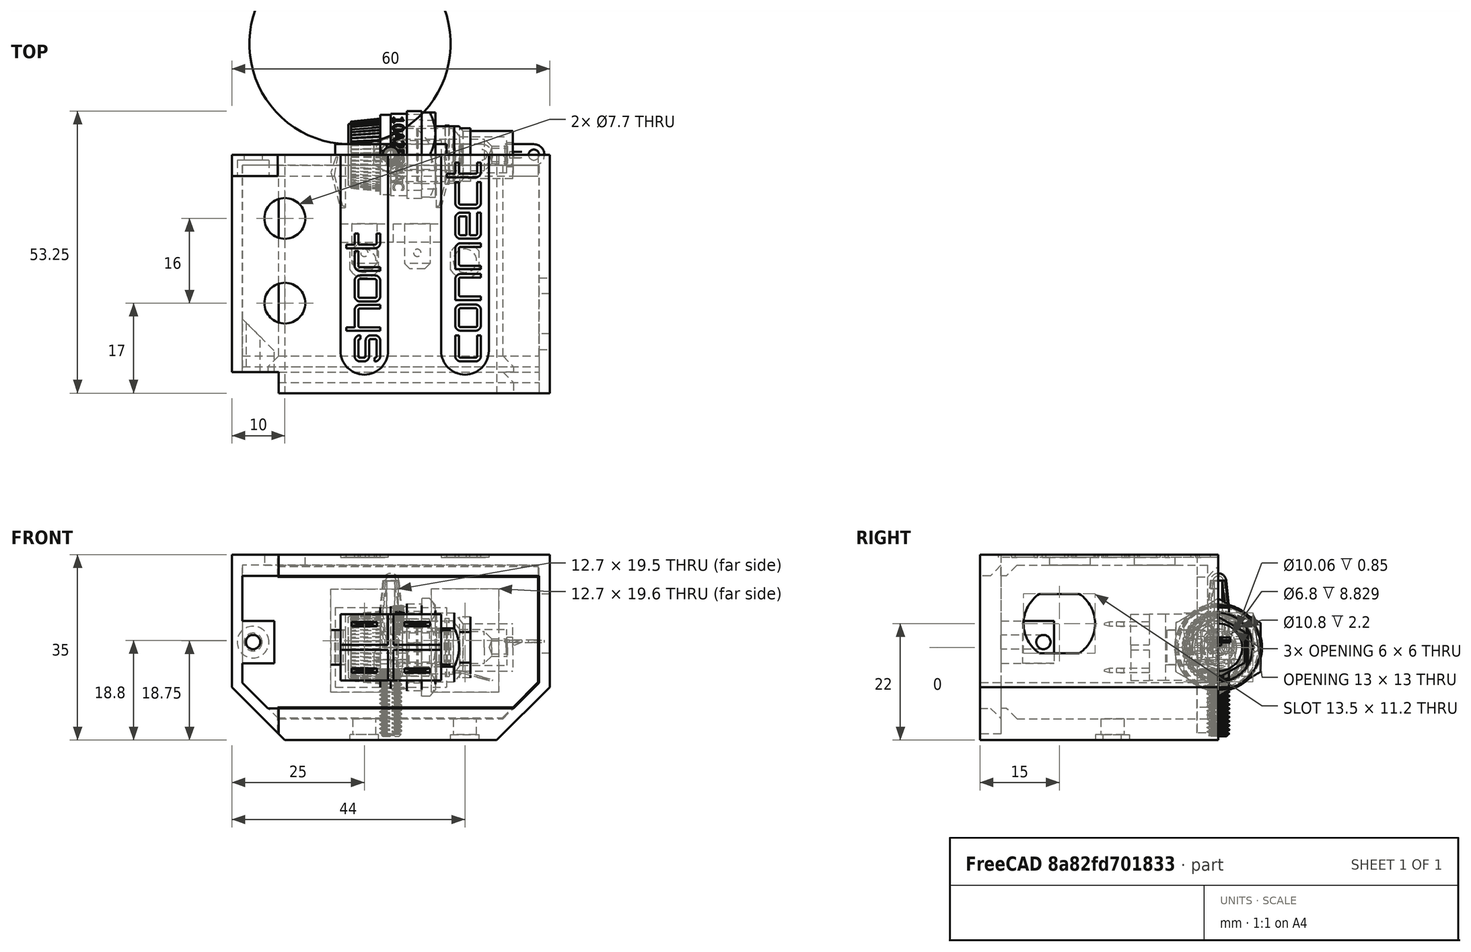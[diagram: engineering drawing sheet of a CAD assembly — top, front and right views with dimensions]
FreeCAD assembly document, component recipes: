
FREECAD ASSEMBLY — COMPONENT RECIPES ("multimeter_module")

This assembly document has 9 components, labeled P0..P8 below (a component is one placed body or linked part). 9 of them carry a construction recipe — the FreeCAD feature program that regenerates the part from scratch, quoted from this document or its linked companion documents; the rest are supplied as boundary geometry only. No exploded tour is included for this assembly.
COMPONENT P0 — recipe-attached ("Box001", modeled in this document).
Construction recipe (the document's own serialized feature program — sketch geometry with constraints, then the solid features built on it; lengths are millimeters unless a unit is written):

FEATURE [Sketcher::SketchObject] Sketch
  ArcFitTolerance = 1e-06
  AttachmentSupport = -> [XZ_Plane]
  FullyConstrained = true
  MakeInternals = false
  MapMode = 5
  Placement = pos=(0,0,0) rot=(1,0,0;1.5708rad)
  expr: Constraints[10] = Spreadsheet.Height
  expr: Constraints[9] = Spreadsheet.Length
  sketch-geometry (5):
    g0: LineSegment StartX=-30 StartY=-17.5 StartZ=0 EndX=30 EndY=-17.5 EndZ=0
    g1: LineSegment StartX=30 StartY=-17.5 StartZ=0 EndX=30 EndY=17.5 EndZ=0
    g2: LineSegment StartX=30 StartY=17.5 StartZ=0 EndX=-30 EndY=17.5 EndZ=0
    g3: LineSegment StartX=-30 StartY=17.5 StartZ=0 EndX=-30 EndY=-17.5 EndZ=0
    g4: GeomPoint [constr] X=0 Y=0 Z=0
  constraints (12):
    c: Coincident(g0,g1)
    c: Coincident(g1,g2)
    c: Coincident(g2,g3)
    c: Coincident(g3,g0)
    c: Horizontal(g0)
    c: Horizontal(g2)
    c: Vertical(g1)
    c: Vertical(g3)
    c: Symmetric(g2,g0,g4)
    c: Distance(g1,g3) = 60
    c: Distance(g0,g2) = 35
    c: Coincident(g4,g-1)
FEATURE [PartDesign::Pad] Pad
  Direction = (0,-1,2e-16)
  Length = 45
  Length2 = 10
  Placement = pos=(0,0,0) rot=(1,0,0;1.5708rad)
  Profile = -> Sketch
  ReferenceAxis = -> Sketch [N_Axis]
  Refine = true
  Suppressed = false
  Type = 0
  expr: Length = Spreadsheet.Width
FEATURE [Sketcher::SketchObject] Sketch001
  ArcFitTolerance = 1e-06
  AttachmentSupport = -> [Pad]
  ExternalGeometry = -> [Pad]
  FullyConstrained = true
  MakeInternals = false
  MapMode = 5
  Placement = pos=(0,-45,0) rot=(1,0,0;1.5708rad)
  expr: Constraints[10] = Spreadsheet.Length - 2 * Spreadsheet.Thickness
  expr: Constraints[11] = Spreadsheet.Thickness
  expr: Constraints[12] = Spreadsheet.Thickness
  expr: Constraints[9] = Spreadsheet.Height - Spreadsheet.Thickness - Spreadsheet.ThicknessBottom
  sketch-geometry (5):
    g0: LineSegment StartX=28 StartY=-13.5 StartZ=0 EndX=28 EndY=15.5 EndZ=0
    g1: LineSegment StartX=28 StartY=15.5 StartZ=0 EndX=-28 EndY=15.5 EndZ=0
    g2: LineSegment StartX=-28 StartY=15.5 StartZ=0 EndX=-28 EndY=-13.5 EndZ=0
    g3: LineSegment StartX=-28 StartY=-13.5 StartZ=0 EndX=28 EndY=-13.5 EndZ=0
    g4: GeomPoint [constr] X=0 Y=0 Z=0
  constraints (13):
    c: Coincident(g0,g1)
    c: Coincident(g1,g2)
    c: Coincident(g2,g3)
    c: Coincident(g3,g0)
    c: Vertical(g0)
    c: Vertical(g2)
    c: Horizontal(g1)
    c: Horizontal(g3)
    c: Coincident(g4,g-1)
    c: DistanceY(g0,g0) = 29
    c: DistanceX(g3,g3) = 56
    c: Distance(g-4,g1) = 2
    c: Distance(g-3,g2) = 2
FEATURE [PartDesign::Pocket] Pocket  label="Box inside"
  BaseFeature = -> Pad
  Direction = (0,1,-2e-16)
  Length = 43
  Length2 = 5
  Placement = pos=(0,0,0) rot=(1,0,0;1.5708rad)
  Profile = -> Sketch001
  ReferenceAxis = -> Sketch001 [N_Axis]
  Refine = true
  Suppressed = false
  Type = 0
  expr: Length = Spreadsheet.Width - Spreadsheet.Thickness
FEATURE [Sketcher::SketchObject] Sketch003
  ArcFitTolerance = 1e-06
  AttachmentSupport = -> [Pocket]
  ExternalGeometry = -> [Pocket]
  FullyConstrained = true
  MakeInternals = false
  MapMode = 5
  Placement = pos=(0,0,0) rot=(-1,0,0;1.5708rad)
  expr: Constraints[19] = Spreadsheet.SwitchWidth
  expr: Constraints[21] = Spreadsheet.SwitchDistance
  expr: Constraints[26] = Spreadsheet.PlugOffset
  expr: Constraints[8] = Spreadsheet.SwitchWidth
  expr: Constraints[9] = Spreadsheet.SwitchHeight
  sketch-geometry (11):
    g0: LineSegment StartX=7.65 StartY=-11.1 StartZ=0 EndX=20.35 EndY=-11.1 EndZ=0
    g1: LineSegment StartX=20.35 StartY=-11.1 StartZ=0 EndX=20.35 EndY=8.5 EndZ=0
    g2: LineSegment StartX=20.35 StartY=8.5 StartZ=0 EndX=7.65 EndY=8.5 EndZ=0
    g3: LineSegment StartX=7.65 StartY=8.5 StartZ=0 EndX=7.65 EndY=-11.1 EndZ=0
    g4: GeomPoint [constr] X=14 Y=-1.3 Z=0
    g5: LineSegment StartX=-11.35 StartY=-11 StartZ=0 EndX=1.35 EndY=-11 EndZ=0
    g6: LineSegment StartX=1.35 StartY=-11 StartZ=0 EndX=1.35 EndY=8.5 EndZ=0
    g7: LineSegment StartX=1.35 StartY=8.5 StartZ=0 EndX=-11.35 EndY=8.5 EndZ=0
    g8: LineSegment StartX=-11.35 StartY=8.5 StartZ=0 EndX=-11.35 EndY=-11 EndZ=0
    g9: GeomPoint [constr] X=-5 Y=-1.25 Z=0
    g10: LineSegment [constr] StartX=-11.35 StartY=8.5 StartZ=0 EndX=20.35 EndY=8.5 EndZ=0
  constraints (28):
    c: Coincident(g0,g1)
    c: Coincident(g1,g2)
    c: Coincident(g2,g3)
    c: Coincident(g3,g0)
    c: Horizontal(g0)
    c: Horizontal(g2)
    c: Vertical(g1)
    c: Vertical(g3)
    c: Distance(g1,g3) = 12.7
    c: Distance(g0,g2) = 19.6
    c: Coincident(g5,g6)
    c: Coincident(g6,g7)
    c: Coincident(g7,g8)
    c: Coincident(g8,g5)
    c: Horizontal(g5)
    c: Horizontal(g7)
    c: Vertical(g6)
    c: Vertical(g8)
    c: Symmetric(g7,g5,g9) = 13
    c: Distance(g6,g8) = 12.7
    c: Distance(g5,g7) = 19.5
    c: DistanceX(g9,g4) = 19
    c: Distance(g-3,g7) = 9
    c: Coincident(g10,g7)
    c: Coincident(g10,g1)
    c: Horizontal(g10)
    c: Distance(g4,g-4) = 16
    c: Symmetric(g0,g1,g4)
FEATURE [PartDesign::Pocket] Pocket001  label="Switch holes"
  BaseFeature = -> Pocket
  Direction = (0,-1,-2e-16)
  Length = 3
  Length2 = 5
  Placement = pos=(0,0,0) rot=(1,0,0;1.5708rad)
  Profile = -> Sketch003
  ReferenceAxis = -> Sketch003 [N_Axis]
  Refine = true
  Suppressed = false
  Type = 0
  expr: Length = Spreadsheet.Thickness + 1
FEATURE [Sketcher::SketchObject] Sketch004
  ArcFitTolerance = 1e-06
  AttachmentSupport = -> [Pocket001]
  ExternalGeometry = -> [Pocket001]
  FullyConstrained = true
  MakeInternals = false
  MapMode = 5
  Placement = pos=(0,-7.7e-15,-17.5) rot=(1,0,0;3.14159rad)
  expr: Constraints[0] = Spreadsheet.PlugDiameter
  expr: Constraints[1] = Spreadsheet.PlugDiameter
  expr: Constraints[5] = Spreadsheet.PlugOffset
  expr: Constraints[7] = Spreadsheet.PlugDistance
  sketch-geometry (3):
    g0: Circle CenterX=14 CenterY=20 CenterZ=0 NormalX=0 NormalY=0 NormalZ=1 AngleXU=0 Radius=2.2
    g1: Circle CenterX=-5 CenterY=20 CenterZ=0 NormalX=0 NormalY=0 NormalZ=1 AngleXU=0 Radius=2.2
    g2: LineSegment [constr] StartX=-5 StartY=20 StartZ=0 EndX=14 EndY=20 EndZ=0
  constraints (8):
    c: Diameter(g0) = 4.4
    c: Diameter(g1) = 4.4
    c: Coincident(g2,g1)
    c: Coincident(g2,g0)
    c: Horizontal(g2)
    c: Distance(g0,g-4) = 16
    c: DistanceY(g-1,g0) = 20
    c: DistanceX(g1,g0) = 19
FEATURE [PartDesign::Pocket] Pocket002  label="Plug holes"
  BaseFeature = -> Pocket001
  Direction = (0,0,1)
  Length = 5
  Length2 = 5
  Placement = pos=(0,0,0) rot=(1,0,0;1.5708rad)
  Profile = -> Sketch004
  ReferenceAxis = -> Sketch004 [N_Axis]
  Refine = true
  Suppressed = false
  Type = 0
  expr: Length = Spreadsheet.ThicknessBottom + 1
FEATURE [Sketcher::SketchObject] Sketch005
  ArcFitTolerance = 1e-06
  AttachmentSupport = -> [Pocket002]
  ExternalGeometry = -> [Pocket002]
  FullyConstrained = true
  MakeInternals = false
  MapMode = 5
  Placement = pos=(0,7.7e-15,17.5) rot=(0,0,1;3.14159rad)
  expr: Constraints[0] = Spreadsheet.SocketDiameter
  expr: Constraints[1] = Spreadsheet.SocketDiameter
  expr: Constraints[5] = Spreadsheet.SocketDistance
  sketch-geometry (3):
    g0: Circle CenterX=20 CenterY=28 CenterZ=0 NormalX=0 NormalY=0 NormalZ=1 AngleXU=0 Radius=3.85
    g1: Circle CenterX=20 CenterY=12 CenterZ=0 NormalX=0 NormalY=0 NormalZ=1 AngleXU=0 Radius=3.85
    g2: LineSegment [constr] StartX=20 StartY=28 StartZ=0 EndX=20 EndY=12 EndZ=0
  constraints (8):
    c: Diameter(g0) = 7.7
    c: Diameter(g1) = 7.7
    c: Coincident(g2,g0)
    c: Coincident(g2,g1)
    c: Vertical(g2)
    c: DistanceY(g1,g0) = 16
    c: Distance(g1,g-1) = 12
    c: Distance(g0,g-3) = 50
FEATURE [PartDesign::Pocket] Pocket003  label="Socket holes"
  BaseFeature = -> Pocket002
  Direction = (0,0,-1)
  Length = 3
  Length2 = 5
  Placement = pos=(0,0,0) rot=(1,0,0;1.5708rad)
  Profile = -> Sketch005
  ReferenceAxis = -> Sketch005 [N_Axis]
  Refine = true
  Suppressed = false
  Type = 0
  expr: Length = Spreadsheet.Thickness + 1
FEATURE [Sketcher::SketchObject] Sketch006
  ArcFitTolerance = 1e-06
  AttachmentSupport = -> [Pocket003]
  ExternalGeometry = -> [Pocket003]
  FullyConstrained = true
  MakeInternals = false
  MapMode = 5
  Placement = pos=(30,0,0) rot=(0.707107,0,0.707107;3.14159rad)
  expr: Constraints[11] = Spreadsheet.FuseHeight / 2
  expr: Constraints[12] = Spreadsheet.FuseHeight / 2
  expr: Constraints[1] = Spreadsheet.FuseWidth
  sketch-geometry (4):
    g0: LineSegment StartX=-1.1 StartY=33.7686 StartZ=0 EndX=-1.1 EndY=26.2314 EndZ=0
    g1: LineSegment StartX=10.1 StartY=33.7686 StartZ=0 EndX=10.1 EndY=26.2314 EndZ=0
    g2: ArcOfCircle CenterX=4.5 CenterY=30 CenterZ=0 NormalX=0 NormalY=0 NormalZ=1 AngleXU=0 Radius=6.75 StartAngle=0.592352 EndAngle=2.54924
    g3: ArcOfCircle CenterX=4.5 CenterY=30 CenterZ=0 NormalX=0 NormalY=0 NormalZ=1 AngleXU=0 Radius=6.75 StartAngle=3.73394 EndAngle=5.69083
  constraints (13):
    c: Coincident(g3,g2)
    c: Distance(g0,g1) = 11.2
    c: Distance(g2,g-3) = 22
    c: Vertical(g0)
    c: Vertical(g1)
    c: Distance(g2,g-4) = 30
    c: Equal(g0,g1)
    c: Coincident(g1,g2)
    c: Coincident(g1,g3)
    c: Coincident(g0,g3)
    c: Coincident(g0,g2)
    c: Radius(g3) = 6.75
    c: Radius(g2) = 6.75
FEATURE [PartDesign::Pocket] Pocket004  label="Fuse hole"
  BaseFeature = -> Pocket003
  Direction = (-1,0,2e-16)
  Length = 5
  Length2 = 5
  Placement = pos=(0,0,0) rot=(1,0,0;1.5708rad)
  Profile = -> Sketch006
  ReferenceAxis = -> Sketch006 [N_Axis]
  Refine = true
  Suppressed = false
  Type = 0
  expr: Length = Spreadsheet.ThicknessBottom + 1
FEATURE [Sketcher::SketchObject] Sketch007
  ArcFitTolerance = 1e-06
  AttachmentSupport = -> [Pocket004]
  ExternalGeometry = -> [Pocket004]
  FullyConstrained = true
  MakeInternals = false
  MapMode = 5
  Placement = pos=(0,-7.7e-15,-17.5) rot=(1,0,0;3.14159rad)
  expr: Constraints[13] = Spreadsheet.PlugPocketLength
  expr: Constraints[22] = Spreadsheet.PlugPocketWidth
  expr: Constraints[23] = Spreadsheet.PlugPocketWidth
  expr: Constraints[3] = Spreadsheet.PlugPocketLength
  sketch-geometry (8):
    g0: LineSegment StartX=11.3 StartY=21.7176 StartZ=0 EndX=11.3 EndY=18.2824 EndZ=0
    g1: LineSegment StartX=16.7 StartY=21.7176 StartZ=0 EndX=16.7 EndY=18.2824 EndZ=0
    g2: ArcOfCircle CenterX=14 CenterY=20 CenterZ=0 NormalX=0 NormalY=0 NormalZ=1 AngleXU=0 Radius=3.2 StartAngle=3.70816 EndAngle=5.71662
    g3: ArcOfCircle CenterX=14 CenterY=20 CenterZ=0 NormalX=0 NormalY=0 NormalZ=1 AngleXU=0 Radius=3.2 StartAngle=0.566564 EndAngle=2.57503
    g4: LineSegment StartX=-7.7 StartY=21.7176 StartZ=0 EndX=-7.7 EndY=18.2824 EndZ=0
    g5: LineSegment StartX=-2.3 StartY=21.7176 StartZ=0 EndX=-2.3 EndY=18.2824 EndZ=0
    g6: ArcOfCircle CenterX=-5 CenterY=20 CenterZ=0 NormalX=0 NormalY=0 NormalZ=1 AngleXU=0 Radius=3.2 StartAngle=3.70816 EndAngle=5.71662
    g7: ArcOfCircle CenterX=-5 CenterY=20 CenterZ=0 NormalX=0 NormalY=0 NormalZ=1 AngleXU=0 Radius=3.2 StartAngle=0.566564 EndAngle=2.57503
  constraints (26):
    c: Vertical(g0)
    c: Vertical(g1)
    c: Coincident(g2,g-4)
    c: Diameter(g2) = 6.4
    c: PointOnObject(g1,g3)
    c: Coincident(g3,g0)
    c: Coincident(g2,g0)
    c: Equal(g2,g3)
    c: Coincident(g2,g1)
    c: PointOnObject(g3,g1)
    c: Coincident(g2,g3)
    c: Vertical(g5)
    c: Vertical(g4)
    c: Diameter(g6) = 6.4
    c: Coincident(g6,g-3)
    c: PointOnObject(g5,g7)
    c: Coincident(g7,g4)
    c: Coincident(g6,g4)
    c: Equal(g6,g7)
    c: Coincident(g6,g5)
    c: PointOnObject(g7,g5)
    c: Coincident(g6,g7)
    c: Distance(g1,g0) = 5.4
    c: Distance(g5,g4) = 5.4
    c: Equal(g4,g5)
    c: Equal(g0,g1)
FEATURE [PartDesign::Pocket] Pocket005  label="Plug pockets"
  AttacherType = Attacher::AttachEngine3D
  BaseFeature = -> Pocket004
  Direction = (0,0,1)
  Length = 1
  Length2 = 5
  Placement = pos=(0,0,0) rot=(1,0,0;1.5708rad)
  Profile = -> Sketch007
  ReferenceAxis = -> Sketch007 [N_Axis]
  Refine = true
  Suppressed = false
  Type = 0
FEATURE [Sketcher::SketchObject] Sketch008
  ArcFitTolerance = 1e-06
  AttachmentSupport = -> [Pocket005]
  ExternalGeometry = -> [Pocket005]
  FullyConstrained = true
  MakeInternals = false
  MapMode = 5
  Placement = pos=(0,0,0) rot=(-1,0,0;1.5708rad)
  expr: Constraints[6] = Spreadsheet.PullChamferDepth
  expr: Constraints[7] = Spreadsheet.PullChamferDepth
  sketch-geometry (3):
    g0: LineSegment StartX=30 StartY=17.5 StartZ=0 EndX=30 EndY=7.5 EndZ=0
    g1: LineSegment StartX=30 StartY=17.5 StartZ=0 EndX=20 EndY=17.5 EndZ=0
    g2: LineSegment StartX=20 StartY=17.5 StartZ=0 EndX=30 EndY=7.5 EndZ=0
  constraints (8):
    c: Coincident(g0,g-4)
    c: PointOnObject(g0,g-4)
    c: Coincident(g1,g0)
    c: Horizontal(g1)
    c: Coincident(g2,g1)
    c: Coincident(g2,g0)
    c: DistanceY(g0,g0) = 10
    c: DistanceX(g1,g0) = 10
FEATURE [PartDesign::Plane] DatumPlane  label="Lid shelves symmetry plane"
  AttachmentOffset = pos=(0,0,14.5) rot=(0,0,1;0rad)
  Length = 72.9615
  MapMode = 5
  Placement = pos=(0,6.8e-15,1) rot=(1,0,0;3.14159rad)
  ResizeMode = 0
  Width = 82.9615
  expr: .AttachmentOffset.Base.z = (Spreadsheet.Height - Spreadsheet.Thickness - Spreadsheet.ThicknessBottom) / 2
FEATURE [Sketcher::SketchObject] Sketch013
  ArcFitTolerance = 1e-06
  FullyConstrained = true
  MakeInternals = false
  MapMode = 5
  Placement = pos=(0,7.7e-15,17.5) rot=(0,0,1;3.14159rad)
  sketch-geometry (4):
    g0: LineSegment StartX=30 StartY=45 StartZ=0 EndX=21.1716 EndY=45 EndZ=0
    g1: LineSegment StartX=21.1716 StartY=45 StartZ=0 EndX=21.1716 EndY=41 EndZ=0
    g2: LineSegment StartX=21.1716 StartY=41 StartZ=0 EndX=30 EndY=41 EndZ=0
    g3: LineSegment StartX=30 StartY=41 StartZ=0 EndX=30 EndY=45 EndZ=0
  constraints (10):
    c: Coincident(g0,g1)
    c: Coincident(g1,g2)
    c: Coincident(g2,g3)
    c: Coincident(g3,g0)
    c: Horizontal(g0)
    c: Horizontal(g2)
    c: Vertical(g1)
    c: Vertical(g3)
    c: Coincident(g0,g-4)
    c: Coincident(g1,g-5)
FEATURE [Sketcher::SketchObject] Sketch014
  ArcFitTolerance = 1e-06
  AttachmentSupport = -> [DatumPlane]
  FullyConstrained = true
  MakeInternals = false
  MapMode = 5
  Placement = pos=(0,6.8e-15,1) rot=(1,0,0;3.14159rad)
  sketch-geometry (4):
    g0: LineSegment StartX=-28 StartY=41 StartZ=0 EndX=-22 EndY=41 EndZ=0
    g1: LineSegment StartX=-22 StartY=41 StartZ=0 EndX=-22 EndY=37 EndZ=0
    g2: LineSegment StartX=-28 StartY=41 StartZ=0 EndX=-28 EndY=31 EndZ=0
    g3: LineSegment StartX=-28 StartY=31 StartZ=0 EndX=-22 EndY=37 EndZ=0
  constraints (11):
    c: Coincident(g0,g-4)
    c: PointOnObject(g0,g-4)
    c: Coincident(g1,g0)
    c: Parallel(g2,g-3)
    c: Coincident(g2,g0)
    c: Coincident(g3,g2)
    c: Coincident(g3,g1)
    c: DistanceX(g0,g0) = 6
    c: Vertical(g1)
    c: Angle(g3,g2) = 0.785398
    c: DistanceY(g1,g0) = 4
FEATURE [Sketcher::SketchObject] Sketch021
  ArcFitTolerance = 1e-06
  AttachmentSupport = -> [Pocket005]
  ExternalGeometry = -> [Pocket005]
  FullyConstrained = true
  MakeInternals = false
  MapMode = 5
  Placement = pos=(-28,0,0) rot=(0.707107,0,0.707107;3.14159rad)
  sketch-geometry (7):
    g0: LineSegment StartX=-13.5 StartY=45 StartZ=0 EndX=-11.5 EndY=45 EndZ=0
    g1: LineSegment StartX=-11.5 StartY=45 StartZ=0 EndX=-11.5 EndY=43 EndZ=0
    g2: LineSegment StartX=-11.5 StartY=43 StartZ=0 EndX=-13.5 EndY=41 EndZ=0
    g3: LineSegment StartX=-13.5 StartY=41 StartZ=0 EndX=-11.5 EndY=41 EndZ=0
    g4: LineSegment StartX=-11.5 StartY=41 StartZ=0 EndX=-11.5 EndY=40 EndZ=0
    g5: LineSegment StartX=-11.5 StartY=40 StartZ=0 EndX=-13.5 EndY=38 EndZ=0
    g6: LineSegment StartX=-13.5 StartY=38 StartZ=0 EndX=-13.5 EndY=45 EndZ=0
  constraints (20):
    c: Coincident(g0,g-4)
    c: Coincident(g1,g0)
    c: Vertical(g1)
    c: Coincident(g2,g1)
    c: PointOnObject(g2,g-4)
    c: Coincident(g3,g2)
    c: Horizontal(g3)
    c: Coincident(g4,g3)
    c: Vertical(g4)
    c: Coincident(g5,g4)
    c: PointOnObject(g5,g-4)
    c: Coincident(g6,g5)
    c: Coincident(g6,g0)
    c: Horizontal(g0)
    c: Angle(g2,g6) = 0.785398
    c: Angle(g5,g6) = 0.785398
    c: DistanceX(g0,g0) = 2
    c: DistanceY(g1,g0) = 2
    c: Distance(g3,g4) = 1
    c: Equal(g0,g3)
FEATURE [PartDesign::Pad] Pad007  label="Lid shelf right"
  BaseFeature = -> Pocket005
  Direction = (1,0,-2e-16)
  Length = 10
  Length2 = 10
  Placement = pos=(0,0,0) rot=(1,0,0;1.5708rad)
  Profile = -> Sketch021
  ReferenceAxis = -> Sketch021 [N_Axis]
  Refine = true
  Suppressed = false
  Type = 1
FEATURE [PartDesign::Mirrored] Mirrored  label="Lid shelf left"
  BaseFeature = -> Pad007
  MirrorPlane = -> DatumPlane
  Originals = -> [Pad007]
  Placement = pos=(0,0,0) rot=(1,0,0;1.5708rad)
  Refine = true
  Suppressed = false
  TransformMode = 0
FEATURE [PartDesign::Pocket] Pocket006  label="Pull chamfer left"
  BaseFeature = -> Mirrored
  Direction = (0,-1,-2e-16)
  Length = 47
  Length2 = 5
  Placement = pos=(0,0,0) rot=(1,0,0;1.5708rad)
  Profile = -> Sketch008
  ReferenceAxis = -> Sketch008 [N_Axis]
  Refine = true
  Suppressed = false
  Type = 1
  expr: Length = Spreadsheet.Width + 2
FEATURE [Sketcher::SketchObject] Sketch009
  ArcFitTolerance = 1e-06
  AttachmentSupport = -> [Pocket006]
  ExternalGeometry = -> [Pocket006]
  FullyConstrained = true
  MakeInternals = false
  MapMode = 5
  Placement = pos=(0,0,0) rot=(-1,0,0;1.5708rad)
  expr: Constraints[9] = Spreadsheet.Thickness
  sketch-geometry (4):
    g0: LineSegment StartX=20 StartY=17.5 StartZ=0 EndX=30 EndY=7.5 EndZ=0
    g1: LineSegment StartX=20 StartY=17.5 StartZ=0 EndX=17.1716 EndY=17.5 EndZ=0
    g2: LineSegment StartX=30 StartY=7.5 StartZ=0 EndX=30 EndY=4.67157 EndZ=0
    g3: LineSegment StartX=17.1716 StartY=17.5 StartZ=0 EndX=30 EndY=4.67157 EndZ=0
  constraints (10):
    c: Coincident(g0,g-4)
    c: Coincident(g0,g-5)
    c: Coincident(g1,g0)
    c: PointOnObject(g1,g-3)
    c: Coincident(g2,g0)
    c: PointOnObject(g2,g-5)
    c: Coincident(g3,g1)
    c: Coincident(g3,g2)
    c: Parallel(g0,g3)
    c: Distance(g3,g0) = 2
FEATURE [PartDesign::Pad] Pad001  label="Pull chamfer left wall"
  BaseFeature = -> Pocket006
  Direction = (0,1,2e-16)
  Length = 45
  Length2 = 10
  Placement = pos=(0,0,0) rot=(1,0,0;1.5708rad)
  Profile = -> Sketch009
  ReferenceAxis = -> Sketch009 [N_Axis]
  Refine = true
  Reversed = true
  Suppressed = false
  Type = 1
  expr: Length = Spreadsheet.Width
FEATURE [PartDesign::Mirrored] Mirrored001  label="Pull chamfer right"
  BaseFeature = -> Pad001
  MirrorPlane = -> YZ_Plane
  Originals = -> [Pocket006]
  Placement = pos=(0,0,0) rot=(1,0,0;1.5708rad)
  Refine = true
  Suppressed = false
  TransformMode = 0
FEATURE [PartDesign::Mirrored] Mirrored002  label="Pull chamfer right wall"
  BaseFeature = -> Mirrored001
  MirrorPlane = -> YZ_Plane
  Originals = -> [Pad001]
  Placement = pos=(0,0,0) rot=(1,0,0;1.5708rad)
  Refine = true
  Suppressed = false
  TransformMode = 0
FEATURE [PartDesign::Pocket] Pocket008  label="Lid entrance"
  BaseFeature = -> Mirrored002
  Direction = (0,0,-1)
  Length = 5
  Length2 = 5
  Placement = pos=(0,0,0) rot=(1,0,0;1.5708rad)
  Profile = -> Sketch013
  ReferenceAxis = -> Sketch013 [N_Axis]
  Refine = true
  Suppressed = false
  Type = 1
FEATURE [PartDesign::Pad] Pad004  label="Screw holder"
  BaseFeature = -> Pocket008
  Direction = (0,0,-1)
  Length = 8
  Length2 = 10
  Midplane = true
  Placement = pos=(0,0,0) rot=(1,0,0;1.5708rad)
  Profile = -> Sketch014
  ReferenceAxis = -> Sketch014 [N_Axis]
  Refine = true
  Suppressed = false
  Type = 0
FEATURE [Sketcher::SketchObject] Sketch015
  ArcFitTolerance = 1e-06
  AttachmentSupport = -> [Pad004]
  ExternalGeometry = -> [Pad004]
  FullyConstrained = true
  MakeInternals = false
  MapMode = 5
  Placement = pos=(6.0955e-12,-41,1.341e-13) rot=(1,0,0;1.5708rad)
  expr: Constraints[9] = Spreadsheet.ThreadedHoleDiameter
  sketch-geometry (7):
    g0: LineSegment [constr] StartX=-22 StartY=5 StartZ=0 EndX=-30 EndY=5 EndZ=0
    g1: LineSegment [constr] StartX=-22 StartY=-3 StartZ=0 EndX=-30 EndY=-3 EndZ=0
    g2: LineSegment [constr] StartX=-22 StartY=5 StartZ=0 EndX=-30 EndY=-3 EndZ=0
    g3: LineSegment [constr] StartX=-22 StartY=-3 StartZ=0 EndX=-30 EndY=5 EndZ=0
    g4: GeomPoint [constr] X=-26 Y=1 Z=0
    g5: Circle CenterX=-26 CenterY=1 CenterZ=0 NormalX=0 NormalY=0 NormalZ=1 AngleXU=0 Radius=1.35
    g6: LineSegment [constr] StartX=-30 StartY=5 StartZ=0 EndX=-30 EndY=-3 EndZ=0
  constraints (15):
    c: Coincident(g0,g-3)
    c: Coincident(g1,g-3)
    c: Horizontal(g0)
    c: Horizontal(g1)
    c: Coincident(g2,g0)
    c: Coincident(g2,g1)
    c: Coincident(g3,g1)
    c: Coincident(g3,g0)
    c: Symmetric(g3,g3,g4)
    c: Diameter(g5) = 2.7
    c: Coincident(g5,g4)
    c: Coincident(g6,g0)
    c: Coincident(g6,g1)
    c: Vertical(g6)
    c: Equal(g0,g6)
FEATURE [PartDesign::Pocket] Pocket009  label="Screw hole001"
  BaseFeature = -> Pad004
  Direction = (-1.487e-13,1,-2.9e-15)
  Length = 5
  Length2 = 5
  Placement = pos=(0,0,0) rot=(1,0,0;1.5708rad)
  Profile = -> Sketch015
  ReferenceAxis = -> Sketch015 [N_Axis]
  Refine = true
  Suppressed = false
  Type = 2
FEATURE [Part::Part2DObjectPython] ShapeString  label="StringShort"  # Draft 2D object (typed FeaturePython)
  FontFile = <userpath>/Documents/3D/multimeter_module/Orbitron-VariableFont_wght.ttf
  Fuse = false
  Justification = 3
  JustificationReference = 0
  KeepLeftMargin = false
  MakeFace = true
  ObliqueAngle = 0
  Placement = pos=(-5,-39,17.5) rot=(0,0,1;1.5708rad)
  ScaleToSize = true
  Size = 6
  String = short
  Tracking = 0
FEATURE [Part::Part2DObjectPython] ShapeString001  label="StringConnect"  # Draft 2D object (typed FeaturePython)
  FontFile = <userpath>/Documents/3D/multimeter_module/Orbitron-VariableFont_wght.ttf
  Fuse = false
  Justification = 3
  JustificationReference = 0
  KeepLeftMargin = false
  MakeFace = true
  ObliqueAngle = 0
  Placement = pos=(14,-39,17.5) rot=(0,0,1;1.5708rad)
  ScaleToSize = true
  Size = 6
  String = connect
  Tracking = 0
FEATURE [Sketcher::SketchObject] Sketch022
  ArcFitTolerance = 1e-06
  AttachmentSupport = -> [Pocket009]
  ExternalGeometry = -> [Pocket009]
  FullyConstrained = true
  MakeInternals = false
  MapMode = 5
  Placement = pos=(0,7.7e-15,17.5) rot=(0,0,1;3.14159rad)
  expr: Constraints[17] = Spreadsheet.PlugDistance
  expr: Constraints[4] = Spreadsheet.PlugOffset
  sketch-geometry (10):
    g0: LineSegment StartX=-18.5 StartY=7.7e-15 StartZ=0 EndX=-18.5 EndY=37 EndZ=0
    g1: LineSegment StartX=-9.5 StartY=7.7e-15 StartZ=0 EndX=-9.5 EndY=37 EndZ=0
    g2: LineSegment [constr] StartX=-14 StartY=7.7e-15 StartZ=0 EndX=-14 EndY=37 EndZ=0
    g3: ArcOfCircle CenterX=-14 CenterY=37 CenterZ=0 NormalX=0 NormalY=0 NormalZ=1 AngleXU=0 Radius=4.5 StartAngle=6e-16 EndAngle=3.14159
    g4: LineSegment [constr] StartX=5 StartY=7.7e-15 StartZ=0 EndX=5 EndY=37 EndZ=0
    g5: LineSegment StartX=0.5 StartY=7.7e-15 StartZ=0 EndX=0.5 EndY=37 EndZ=0
    g6: LineSegment StartX=9.5 StartY=7.7e-15 StartZ=0 EndX=9.5 EndY=37 EndZ=0
    g7: ArcOfCircle CenterX=5 CenterY=37 CenterZ=0 NormalX=0 NormalY=0 NormalZ=1 AngleXU=0 Radius=4.5 StartAngle=-9e-16 EndAngle=3.14159
    g8: LineSegment StartX=-18.5 StartY=7.7e-15 StartZ=0 EndX=-9.5 EndY=7.7e-15 EndZ=0
    g9: LineSegment StartX=0.5 StartY=7.7e-15 StartZ=0 EndX=9.5 EndY=7.7e-15 EndZ=0
  constraints (30):
    c: Vertical(g0)
    c: Vertical(g1)
    c: Vertical(g2)
    c: PointOnObject(g2,g-3)
    c: DistanceX(g-4,g2) = 16
    c: Distance(g2,g2) = 37
    c: PointOnObject(g0,g-3)
    c: Distance(g1,g0) = 9
    c: Symmetric(g1,g0,g2)
    c: Equal(g1,g2)
    c: Coincident(g1,g3)
    c: Coincident(g0,g3)
    c: Coincident(g3,g2)
    c: PointOnObject(g4,g-3)
    c: Vertical(g4)
    c: PointOnObject(g5,g-3)
    c: Vertical(g5)
    c: Distance(g2,g4) = 19
    c: Symmetric(g5,g6,g4)
    c: Equal(g4,g2)
    c: Equal(g5,g2)
    c: Equal(g6,g2)
    c: Coincident(g7,g4)
    c: Coincident(g7,g6)
    c: Coincident(g7,g5)
    c: Distance(g6,g5) = 9
    c: Coincident(g8,g0)
    c: Coincident(g8,g1)
    c: Coincident(g9,g5)
    c: Coincident(g9,g6)
FEATURE [PartDesign::Pocket] Pocket012  label="TextPockets"
  BaseFeature = -> Pocket009
  Direction = (0,0,-1)
  Length = 0.5
  Length2 = 5
  Placement = pos=(0,0,0) rot=(1,0,0;1.5708rad)
  Profile = -> Sketch022
  ReferenceAxis = -> Sketch022 [N_Axis]
  Refine = true
  Suppressed = false
  Type = 0
FEATURE [PartDesign::Body] Body  label="Box0"
  AllowCompound = false
  Group = -> [Sketch,Pad,Sketch001,Pocket,Sketch003,Pocket001,Sketch004,Pocket002,Sketch005,Pocket003,Sketch006,Pocket004,Sketch007,Pocket005,Pad007,Sketch021,DatumPlane,Mirrored,Sketch008,Pocket006,Sketch009,Pad001,Mirrored001,Mirrored002,Sketch013,Pocket008,Sketch014,Pad004,Sketch015,Pocket009,Sketch022,Pocket012,ShapeString001,ShapeString]
  Origin = -> Origin
  Tip = -> Pocket012
COMPONENT P1 — recipe-attached ("Fuse holder", modeled in this document).
Construction recipe (the document's own serialized feature program — sketch geometry with constraints, then the solid features built on it; lengths are millimeters unless a unit is written):

FEATURE [PartDesign::FeatureBase] BaseFeature003
  BaseFeature = -> Part__Feature008
  Suppressed = false
FEATURE [PartDesign::Body] Body002  label="Fuse holder BK8-HTC-603M001"
  AllowCompound = false
  BaseFeature = -> Part__Feature008
  Group = -> [BaseFeature003]
  Origin = -> Origin003
  Tip = -> BaseFeature003
COMPONENT P2 — recipe-attached ("Lid001", modeled in this document).
Construction recipe (the document's own serialized feature program — sketch geometry with constraints, then the solid features built on it; lengths are millimeters unless a unit is written):

FEATURE [PartDesign::ShapeBinder] ShapeBinder
  Support = -> [Pocket009]
  TraceSupport = false
FEATURE [Sketcher::SketchObject] Sketch016
  ArcFitTolerance = 1e-06
  AttachmentSupport = -> [XZ_Plane006]
  ExternalGeometry = -> [ShapeBinder]
  FullyConstrained = true
  MakeInternals = false
  MapMode = 5
  Placement = pos=(0,0,0) rot=(1,0,0;1.5708rad)
  sketch-geometry (11):
    g0: LineSegment StartX=-21.3716 StartY=17.5 StartZ=0 EndX=-30 EndY=17.5 EndZ=0
    g1: LineSegment StartX=-30 StartY=17.5 StartZ=0 EndX=-30 EndY=-7.5 EndZ=0
    g2: LineSegment StartX=-30 StartY=-7.5 StartZ=0 EndX=-21.3716 EndY=-16.1284 EndZ=0
    g3: LineSegment StartX=-21.3716 StartY=15.3 StartZ=0 EndX=27.8 EndY=15.3 EndZ=0
    g4: LineSegment StartX=27.8 StartY=15.3 StartZ=0 EndX=27.8 EndY=-6.58873 EndZ=0
    g5: LineSegment StartX=-21.3716 StartY=-13.3 StartZ=0 EndX=21.0887 EndY=-13.3 EndZ=0
    g6: LineSegment [constr] StartX=-21.1716 StartY=17.5 StartZ=0 EndX=-21.1716 EndY=-16.3284 EndZ=0
    g7: LineSegment [constr] StartX=-21.3716 StartY=-16.1284 StartZ=0 EndX=-21.3716 EndY=17.5 EndZ=0
    g8: LineSegment StartX=-21.3716 StartY=-16.1284 StartZ=0 EndX=-21.3716 EndY=-13.3 EndZ=0
    g9: LineSegment StartX=-21.3716 StartY=15.3 StartZ=0 EndX=-21.3716 EndY=17.5 EndZ=0
    g10: LineSegment StartX=21.0887 StartY=-13.3 StartZ=0 EndX=27.8 EndY=-6.58873 EndZ=0
  constraints (31):
    c: Coincident(g0,g-6)
    c: Coincident(g1,g0)
    c: Coincident(g1,g-7)
    c: Coincident(g2,g1)
    c: Horizontal(g3)
    c: Distance(g-3,g3) = 0.2
    c: Vertical(g4)
    c: Horizontal(g5)
    c: Distance(g4,g-11) = 0.2
    c: Coincident(g3,g4)
    c: Coincident(g6,g-5)
    c: Coincident(g6,g-8)
    c: Vertical(g7)
    c: Distance(g7,g6) = 0.2
    c: Coincident(g2,g7)
    c: Coincident(g0,g7)
    c: PointOnObject(g5,g7)
    c: PointOnObject(g3,g7)
    c: Distance(g5,g-9) = 0.2
    c: Coincident(g8,g2)
    c: Coincident(g8,g5)
    c: Coincident(g9,g3)
    c: Coincident(g9,g0)
    c: Parallel(g10,g-10)
    c: Distance(g-10,g10) = 0.2
    c: PointOnObject(g10,g5)
    c: PointOnObject(g5,g10)
    c: PointOnObject(g10,g4)
    c: PointOnObject(g4,g10)
    c: Parallel(g2,g-7)
    c: Horizontal(g0)
FEATURE [PartDesign::Pad] Pad005
  Direction = (0,-1,2e-16)
  Length = 4
  Length2 = 10
  Placement = pos=(0,0,0) rot=(1,0,0;1.5708rad)
  Profile = -> Sketch016
  ReferenceAxis = -> Sketch016 [N_Axis]
  Refine = true
  Suppressed = false
  Type = 0
FEATURE [PartDesign::Plane] DatumPlane001  label="Side shapes start"
  AttachmentSupport = -> [Pad005]
  Length = 60
  MapMode = 5
  Placement = pos=(-21.3716,0,2.69e-14) rot=(-0.707107,0,0.707107;3.14159rad)
  ResizeMode = 0
  Width = 60
FEATURE [Sketcher::SketchObject] Sketch017
  ArcFitTolerance = 1e-06
  AttachmentSupport = -> [DatumPlane001]
  ExternalGeometry = -> [Sketch016]
  FullyConstrained = true
  MakeInternals = false
  MapMode = 5
  Placement = pos=(-21.3716,0,2.69e-14) rot=(-0.707107,0,0.707107;3.14159rad)
  sketch-geometry (4):
    g0: LineSegment StartX=13.3 StartY=3e-15 StartZ=0 EndX=11.3 EndY=2 EndZ=0
    g1: LineSegment StartX=11.3 StartY=2 StartZ=0 EndX=11.3 EndY=4 EndZ=0
    g2: LineSegment StartX=11.3 StartY=4 StartZ=0 EndX=13.3 EndY=4 EndZ=0
    g3: LineSegment StartX=13.3 StartY=4 StartZ=0 EndX=13.3 EndY=3.1e-15 EndZ=0
  constraints (11):
    c: Vertical(g1)
    c: Coincident(g2,g1)
    c: Coincident(g3,g2)
    c: Coincident(g0,g3)
    c: Angle(g3,g0) = 0.785398
    c: Distance(g0,g1) = 2
    c: Coincident(g1,g0)
    c: Horizontal(g2)
    c: Coincident(g0,g-3)
    c: Vertical(g3)
    c: Equal(g1,g2)
FEATURE [PartDesign::Pocket] Pocket010  label="Left side"
  BaseFeature = -> Pad005
  Direction = (1,0,-1.4e-15)
  Length = 5
  Length2 = 5
  Placement = pos=(0,0,0) rot=(1,0,0;1.5708rad)
  Profile = -> Sketch017
  ReferenceAxis = -> Sketch017 [N_Axis]
  Refine = true
  Suppressed = false
  Type = 1
FEATURE [Sketcher::SketchObject] Sketch018
  ArcFitTolerance = 1e-06
  AttachmentSupport = -> [DatumPlane001]
  ExternalGeometry = -> [Sketch016]
  FullyConstrained = true
  MakeInternals = false
  MapMode = 5
  Placement = pos=(-21.3716,0,2.69e-14) rot=(-0.707107,0,0.707107;3.14159rad)
  sketch-geometry (4):
    g0: LineSegment StartX=-15.3 StartY=4 StartZ=0 EndX=-15.3 EndY=-3.1e-15 EndZ=0
    g1: LineSegment StartX=-15.3 StartY=4 StartZ=0 EndX=-13.3 EndY=4 EndZ=0
    g2: LineSegment StartX=-13.3 StartY=4 StartZ=0 EndX=-13.3 EndY=2 EndZ=0
    g3: LineSegment StartX=-13.3 StartY=2 StartZ=0 EndX=-15.3 EndY=-3.1e-15 EndZ=0
  constraints (11):
    c: Coincident(g1,g0)
    c: Coincident(g2,g1)
    c: Vertical(g2)
    c: Coincident(g3,g2)
    c: Coincident(g3,g0)
    c: Distance(g2,g1) = 2
    c: Angle(g3,g0) = 0.785398
    c: Coincident(g0,g-3)
    c: Vertical(g0)
    c: Horizontal(g1)
    c: Equal(g2,g1)
FEATURE [PartDesign::Pocket] Pocket011  label="Right side"
  BaseFeature = -> Pocket010
  Direction = (1,0,-1.4e-15)
  Length = 5
  Length2 = 5
  Placement = pos=(0,0,0) rot=(1,0,0;1.5708rad)
  Profile = -> Sketch018
  ReferenceAxis = -> Sketch018 [N_Axis]
  Refine = true
  Suppressed = false
  Type = 1
FEATURE [PartDesign::Line] DatumLine001  label="Hole axis"
  AttacherType = Attacher::AttachEngineLine
  AttachmentSupport = -> [ShapeBinder]
  Length = 20
  MapMode = 19
  Placement = pos=(-26,-41,1) rot=(1,0,0;1.5708rad)
  ResizeMode = 0
FEATURE [PartDesign::Plane] DatumPlane002  label="Hole sketch plane"
  AttachmentSupport = -> [DatumLine001]
  Length = 70.1528
  MapMode = 3
  Placement = pos=(-26,-41,1) rot=(1,0,0;3.14159rad)
  ResizeMode = 0
  Width = 78.3528
FEATURE [Sketcher::SketchObject] Sketch020
  ArcFitTolerance = 1e-06
  AttachmentSupport = -> [DatumPlane002]
  ExternalGeometry = -> [Pocket011,DatumLine001]
  FullyConstrained = true
  MakeInternals = false
  MapMode = 5
  Placement = pos=(-26,-41,1) rot=(1,0,0;3.14159rad)
  expr: Constraints[6] = Spreadsheet.ScrewHeadRadius
  expr: Constraints[7] = Spreadsheet.ScrewHoleRadius
  sketch-geometry (6):
    g0: LineSegment StartX=0 StartY=-41 StartZ=0 EndX=0 EndY=-37 EndZ=0
    g1: LineSegment StartX=3 StartY=-40 StartZ=0 EndX=3 EndY=-37 EndZ=0
    g2: LineSegment StartX=3 StartY=-40 StartZ=0 EndX=1.7 EndY=-40 EndZ=0
    g3: LineSegment StartX=1.7 StartY=-41 StartZ=0 EndX=1.7 EndY=-40 EndZ=0
    g4: LineSegment StartX=1.7 StartY=-41 StartZ=0 EndX=0 EndY=-41 EndZ=0
    g5: LineSegment StartX=0 StartY=-37 StartZ=0 EndX=3 EndY=-37 EndZ=0
  constraints (18):
    c: Vertical(g0)
    c: Vertical(g1)
    c: Vertical(g3)
    c: Coincident(g4,g0)
    c: Coincident(g5,g0)
    c: Horizontal(g5)
    c: DistanceX(g0,g1) = 3
    c: DistanceX(g0,g3) = 1.7
    c: DistanceY(g1,g1) = 3
    c: Coincident(g2,g1)
    c: Coincident(g2,g3)
    c: Coincident(g4,g3)
    c: Coincident(g5,g1)
    c: PointOnObject(g0,g-3)
    c: PointOnObject(g0,g-5)
    c: PointOnObject(g3,g-3)
    c: PointOnObject(g0,g-4)
    c: DistanceY(g3,g2) = 1
FEATURE [PartDesign::Groove] Groove  label="Screw hole"
  Angle = 360
  Angle2 = 60
  Axis = (1.49e-13,-1,2.9e-15)
  Base = (-26,-41,1)
  BaseFeature = -> Pocket011
  Placement = pos=(0,0,0) rot=(1,0,0;1.5708rad)
  Profile = -> Sketch020
  ReferenceAxis = -> Sketch020 [V_Axis]
  Refine = true
  Suppressed = false
  Type = 0
FEATURE [PartDesign::Body] Body005  label="Lid"
  AllowCompound = false
  Group = -> [ShapeBinder,Sketch016,Pad005,DatumPlane001,Sketch017,Pocket010,Sketch018,Pocket011,DatumLine001,DatumPlane002,Sketch020,Groove]
  Origin = -> Origin006
  Tip = -> Groove
COMPONENT P3 — recipe-attached ("Plug COM", modeled in this document).
Construction recipe (the document's own serialized feature program — sketch geometry with constraints, then the solid features built on it; lengths are millimeters unless a unit is written):

FEATURE [PartDesign::FeatureBase] BaseFeature002
  BaseFeature = -> Part__Feature009
  Suppressed = false
FEATURE [PartDesign::Body] Body003  label="Plug 4mm"
  AllowCompound = false
  BaseFeature = -> Part__Feature009
  Group = -> [BaseFeature002]
  Origin = -> Origin004
  Tip = -> BaseFeature002
COMPONENT P4 — same part as P3; its construction recipe is shown at P3.
COMPONENT P5 — recipe-attached ("Socket +", modeled in this document).
Construction recipe (the document's own serialized feature program — sketch geometry with constraints, then the solid features built on it; lengths are millimeters unless a unit is written):

FEATURE [PartDesign::FeatureBase] BaseFeature001
  BaseFeature = -> Part__Feature010
  Suppressed = false
FEATURE [PartDesign::Body] Body004  label="Socket 4mm"
  AllowCompound = false
  BaseFeature = -> Part__Feature010
  Group = -> [BaseFeature001]
  Origin = -> Origin005
  Tip = -> BaseFeature001
COMPONENT P6 — same part as P5; its construction recipe is shown at P5.
COMPONENT P7 — recipe-attached ("Switch SHORT", modeled in this document).
Construction recipe (the document's own serialized feature program — sketch geometry with constraints, then the solid features built on it; lengths are millimeters unless a unit is written):

FEATURE [PartDesign::FeatureBase] BaseFeature
  BaseFeature = -> Part__Feature011
  Suppressed = false
FEATURE [PartDesign::Body] Body001  label="Switch a8l-11-15n11"
  AllowCompound = false
  BaseFeature = -> Part__Feature011
  Group = -> [BaseFeature]
  Origin = -> Origin002
  Tip = -> BaseFeature
COMPONENT P8 — same part as P7; its construction recipe is shown at P7.
PROVENANCE & LICENSES
A FreeCAD (.FCStd) document from a public repository crawl; recipes are the document's own serialized feature recipes (and, for linked parts, companion documents' recipes).
License: cc-by-4.0.
